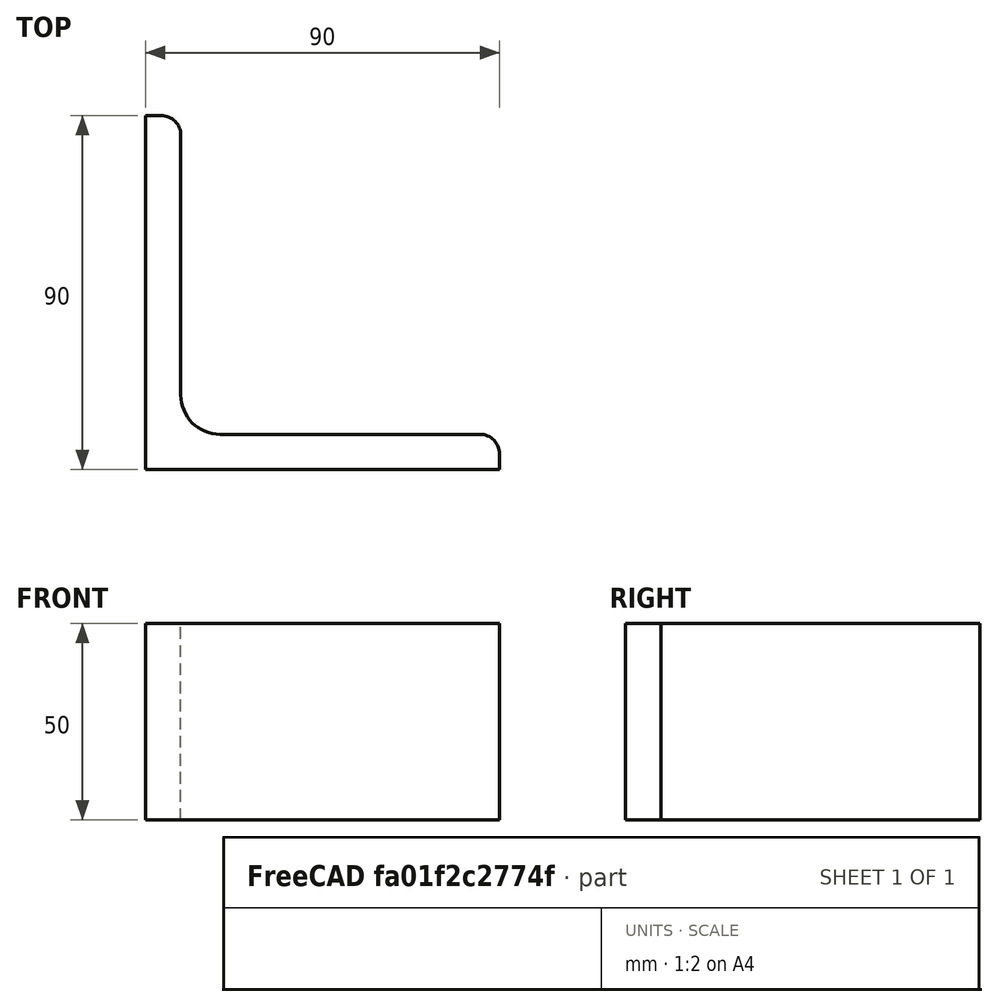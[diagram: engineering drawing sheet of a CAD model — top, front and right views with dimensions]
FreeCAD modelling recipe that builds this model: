
FCSTD DOCUMENT  (FreeCAD 0.15R4671 (Git))
Label: Angle Bar L90x90x9 EN10056 S235JR
License: All rights reserved
LicenseURL: http://en.wikipedia.org/wiki/All_rights_reserved
objects: Sketcher::SketchObject×1, Part::Extrusion×1
note: 2 computed .brp shape members not serialized (recipe doc carries the construction recipe); baked Part::Feature solids carry a one-line shape summary decoded from their .brp

FEATURE [Sketcher::SketchObject] Sketch
  sketch-geometry (9):
    g0: LineSegment StartX=0 StartY=0 StartZ=0 EndX=90 EndY=0 EndZ=0
    g1: LineSegment StartX=90 StartY=0 StartZ=0 EndX=90 EndY=4 EndZ=0
    g2: LineSegment StartX=85 StartY=9 StartZ=0 EndX=19 EndY=9 EndZ=0
    g3: LineSegment StartX=0 StartY=0 StartZ=0 EndX=0 EndY=90 EndZ=0
    g4: LineSegment StartX=0 StartY=90 StartZ=0 EndX=4 EndY=90 EndZ=0
    g5: LineSegment StartX=9 StartY=85 StartZ=0 EndX=9 EndY=19 EndZ=0
    g6: ArcOfCircle CenterX=19 CenterY=19 CenterZ=0 NormalX=0 NormalY=0 NormalZ=1 Radius=10 StartAngle=3.14159 EndAngle=4.71239
    g7: ArcOfCircle CenterX=4 CenterY=85 CenterZ=0 NormalX=0 NormalY=0 NormalZ=1 Radius=5 StartAngle=0 EndAngle=1.5708
    g8: ArcOfCircle CenterX=85 CenterY=4 CenterZ=0 NormalX=0 NormalY=0 NormalZ=1 Radius=5 StartAngle=0 EndAngle=1.5708
  constraints (23):
    c: Coincident(g0,g-1)
    c: Horizontal(g0)
    c: Coincident(g1,g0)
    c: Vertical(g1)
    c: Horizontal(g2)
    c: Coincident(g3,g-1)
    c: Vertical(g3)
    c: Coincident(g4,g3)
    c: Horizontal(g4)
    c: Vertical(g5)
    c: Tangent(g5,g6) = -1.5708
    c: Tangent(g2,g6) = 1.5708
    c: Tangent(g4,g7) = 1.5708
    c: Tangent(g5,g7) = 1.5708
    c: Tangent(g2,g8) = -1.5708
    c: Tangent(g1,g8) = -1.5708
    c: DistanceX(g0) = 90
    c: DistanceY(g3) = 90
    c: DistanceY(g0,g2) = 9
    c: DistanceX(g3,g5) = 9
    c: Radius(g6) = 10
    c: Radius(g8) = 5
    c: Radius(g7) = 5
FEATURE [Part::Extrusion] Extrude  label="Angle Bar L90x90x9 EN10056 S235JR"
  Base = -> Sketch
  Dir = (0,0,50)
  Solid = true
